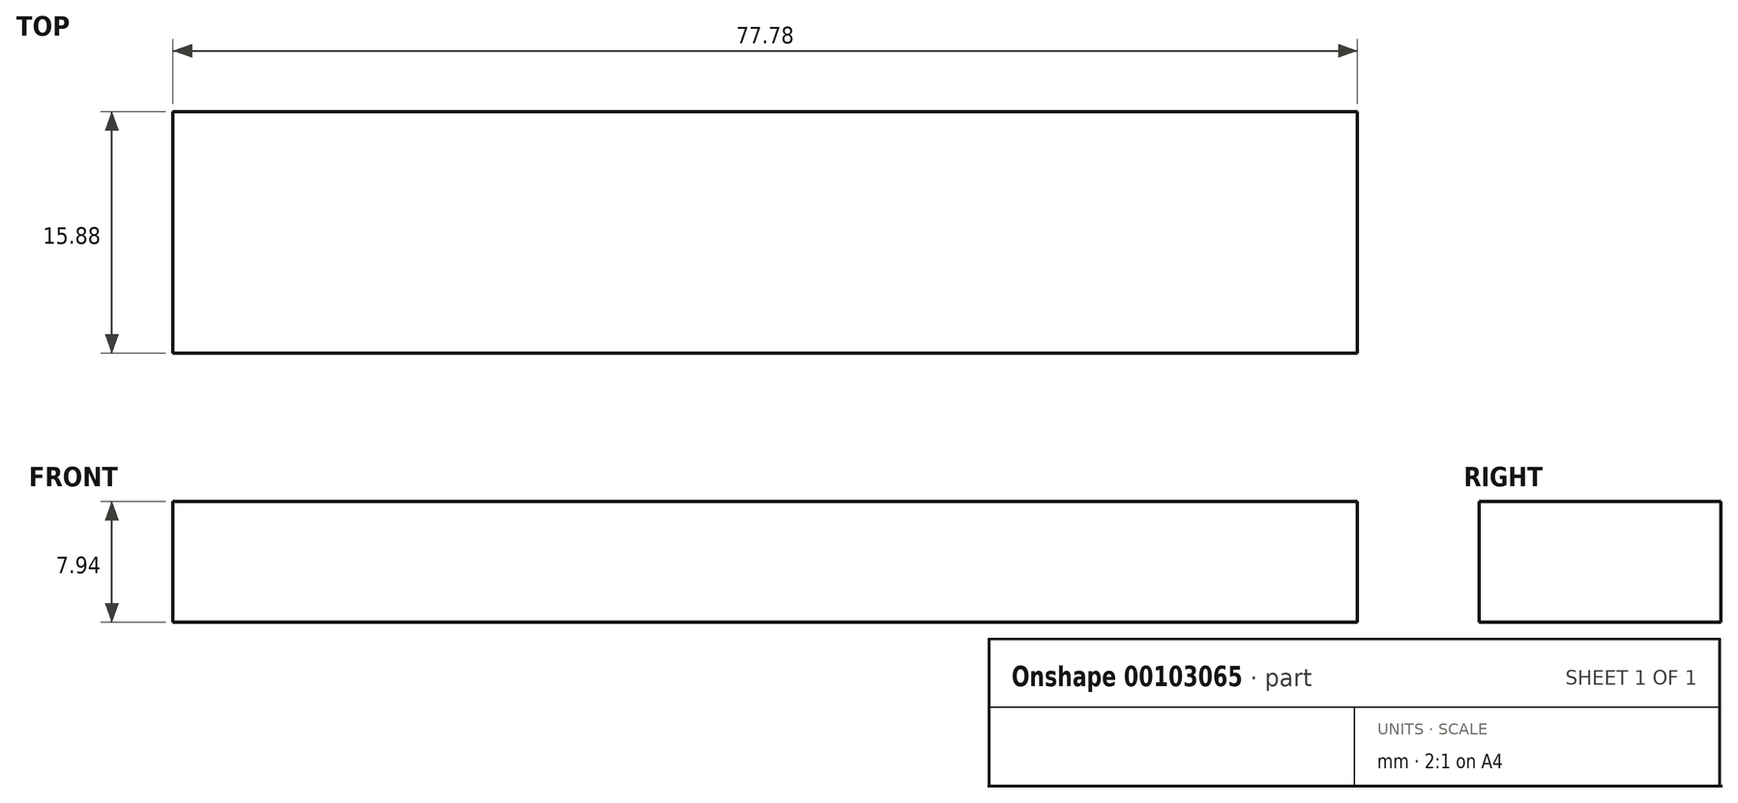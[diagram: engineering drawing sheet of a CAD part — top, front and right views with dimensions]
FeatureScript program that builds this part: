
annotation { "Feature Type Name" : "Feature", "Feature Type Description" : "" }
export const myFeature = defineFeature(function(context is Context, id is Id, definition is map)
    precondition{}
    {
        {
            var Q0;
            Q0=qCreatedBy(makeId("Front.planeOp"),FACE);
            var sketch = newSketch(context, id + "F0", { "sketchPlane" : qUnion([Q0])});
            skLineSegment(sketch, "E0.bottom", {"start": v(-38.9, 3.97) * mm, "end": v(38.9, 3.97) * mm});
            skLineSegment(sketch, "E0.top", {"start": v(-38.9, -3.97) * mm, "end": v(38.9, -3.97) * mm});
            skLineSegment(sketch, "E0.left", {"start": v(-38.9, 3.97) * mm, "end": v(-38.9, -3.97) * mm});
            skLineSegment(sketch, "E0.right", {"start": v(38.9, 3.97) * mm, "end": v(38.9, -3.97) * mm});
            skSolve(sketch);
        }
        {
            var Q0;
            Q0=makeQuery(id+"F0.imprint","IMPRINT",FACE,{"disambiguationData":[TD([[makeQuery(id+"F0.imprint","IMPRINT",EDGE,{"derivedFrom":sQuery(id+"F0.wireOp",EDGE,"E0.bottom")}),-1.0]])]});
            extrude(context, id + "F1", {"entities" : qUnion([Q0]), "depth" : 15.88 * mm});
        }
    });
